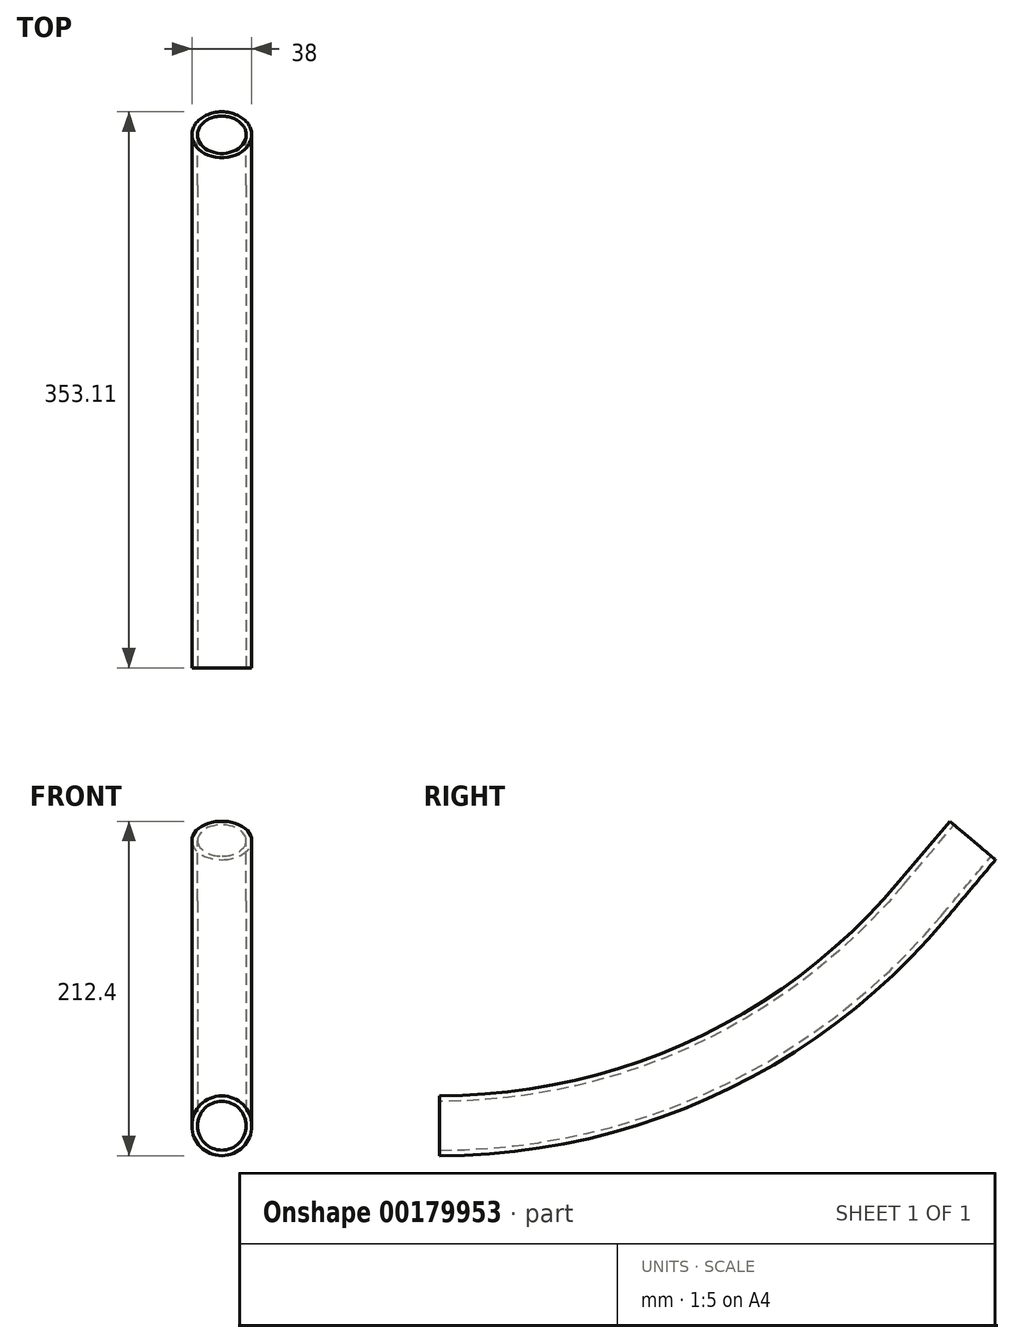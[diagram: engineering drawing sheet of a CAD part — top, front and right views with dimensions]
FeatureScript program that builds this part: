
annotation { "Feature Type Name" : "Feature", "Feature Type Description" : "" }
export const myFeature = defineFeature(function(context is Context, id is Id, definition is map)
    precondition{}
    {
        {
            var Q0;
            Q0=qCreatedBy(makeId("Front.planeOp"),FACE);
            var sketch = newSketch(context, id + "F0", { "sketchPlane" : qUnion([Q0])});
            skCircle(sketch, "E0", {"center": v(0, 0) * mm, "radius": 19 * mm});
            skCircle(sketch, "E1.0", {"center": v(0, 0) * mm, "radius": 15.5 * mm});
            skSolve(sketch);
        }
        {
            var Q0;
            Q0=qCreatedBy(makeId("Right.planeOp"),FACE);
            var sketch = newSketch(context, id + "F1", { "sketchPlane" : qUnion([Q0])});
            skArc(sketch, "E2", {"start": v(0, 0) * mm, "mid": v(169.05, 37.48) * mm, "end": v(306.42, 142.88) * mm});
            skLineSegment(sketch, "E3", {"start": v(306.42, 142.88) * mm, "end": v(338.56, 181.19) * mm});
            skSolve(sketch);
        }
        {
            var Q0;
            Q0=makeQuery(id+"F0.imprint","IMPRINT",FACE,{"disambiguationData":[TD([[makeQuery(id+"F0.imprint","IMPRINT",EDGE,{"derivedFrom":sQuery(id+"F0.wireOp",EDGE,"E0")}),1.0]])]});
            var Q1;
            Q1=sQuery(id+"F1.wireOp",EDGE,"E2");
            var Q2;
            Q2=sQuery(id+"F1.wireOp",EDGE,"E3");
            sweep(context, id + "F2", {"profiles" : qUnion([Q0]), "path" : qUnion([Q1, Q2])});
        }
    });
